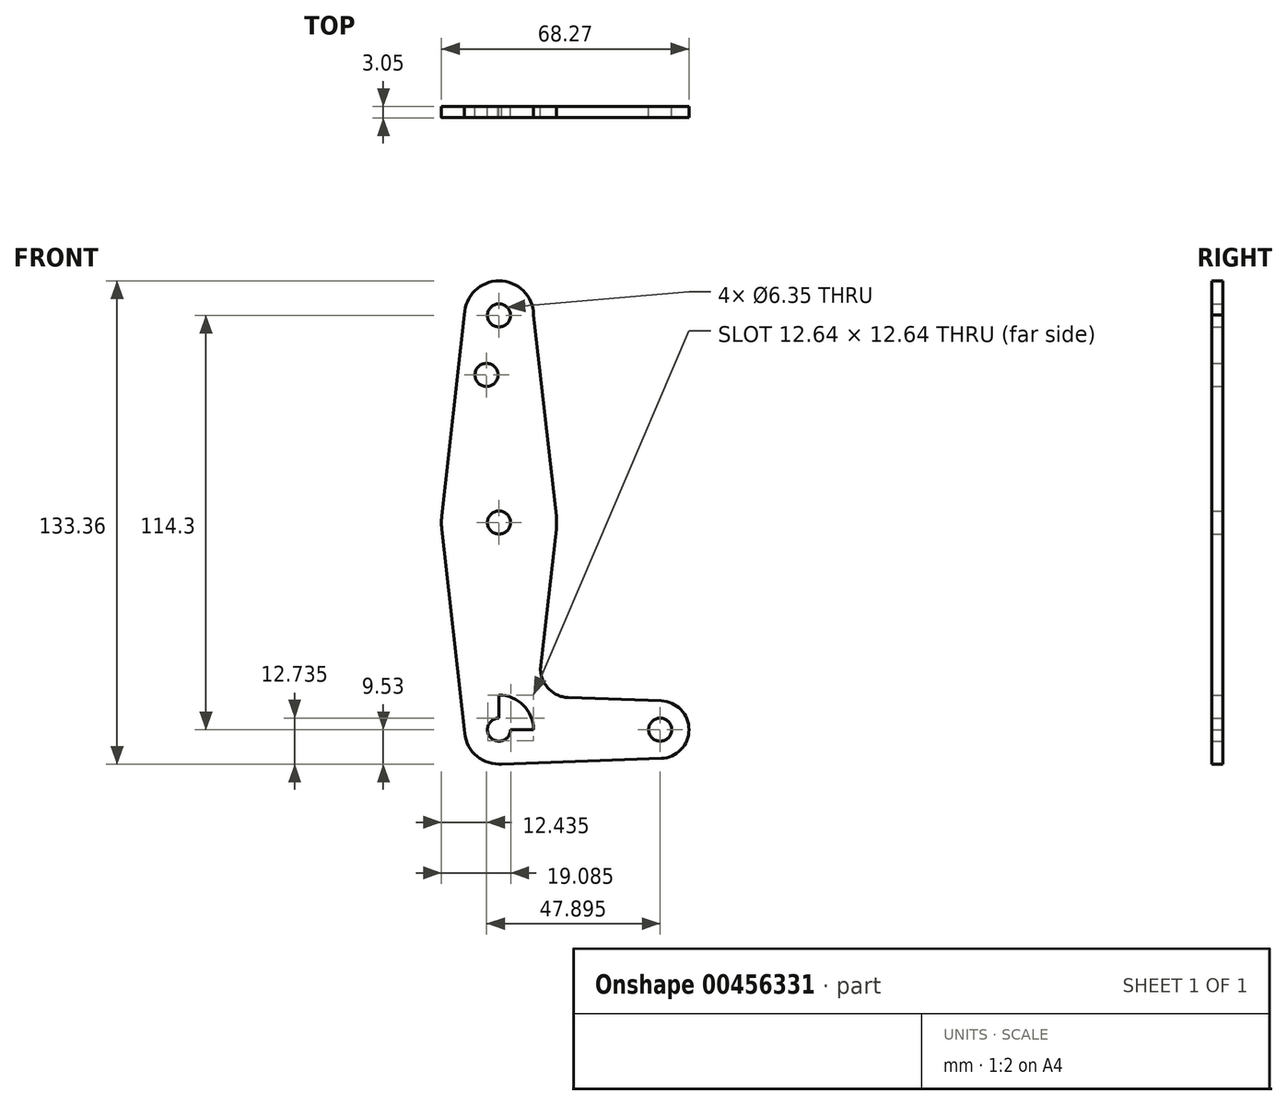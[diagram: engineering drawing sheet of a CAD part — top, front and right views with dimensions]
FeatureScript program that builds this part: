
annotation { "Feature Type Name" : "Feature", "Feature Type Description" : "" }
export const myFeature = defineFeature(function(context is Context, id is Id, definition is map)
    precondition{}
    {
        {
            var Q0;
            Q0=qCreatedBy(makeId("Front.planeOp"),FACE);
            var sketch = newSketch(context, id + "F0", { "sketchPlane" : qUnion([Q0])});
            skCircle(sketch, "E0", {"center": v(0, 0) * mm, "radius": 9.53 * mm});
            skLineSegment(sketch, "E1", {"start": v(0, 0) * mm, "end": v(44.45, 0) * mm});
            skLineSegment(sketch, "E2", {"start": v(0, 114.3) * mm, "end": v(0, 0) * mm});
            skCircle(sketch, "E3", {"center": v(44.45, 0) * mm, "radius": 7.94 * mm});
            skCircle(sketch, "E4", {"center": v(0, 114.3) * mm, "radius": 9.53 * mm});
            skCircle(sketch, "E5", {"center": v(0, 57.15) * mm, "radius": 15.88 * mm});
            skLineSegment(sketch, "E6", {"start": v(19.12, 8.84) * mm, "end": v(44.73, 7.93) * mm});
            skLineSegment(sketch, "E7", {"start": v(0, -9.53) * mm, "end": v(44.73, -7.93) * mm});
            skLineSegment(sketch, "E8", {"start": v(-9.52, 114.5) * mm, "end": v(-15.78, 58.93) * mm});
            skLineSegment(sketch, "E9", {"start": v(9.52, 114.47) * mm, "end": v(15.78, 58.93) * mm});
            skLineSegment(sketch, "E10", {"start": v(11.5, 17.68) * mm, "end": v(15.77, 55.37) * mm});
            skLineSegment(sketch, "E11", {"start": v(-9.53, 0) * mm, "end": v(-15.77, 55.37) * mm});
            skCircle(sketch, "E12", {"center": v(0, 114.3) * mm, "radius": 3.18 * mm});
            skCircle(sketch, "E13", {"center": v(44.45, 0) * mm, "radius": 3.18 * mm});
            skCircle(sketch, "E14", {"center": v(0, 0) * mm, "radius": 3.18 * mm});
            skCircle(sketch, "E15", {"center": v(0, 57.15) * mm, "radius": 3.18 * mm});
            skPoint(sketch, "E16.newPointA", {"position": v(9.52, 0.22) * mm});
            skArc(sketch, "E16.filletArc", {"start": v(11.5, 17.68) * mm, "mid": v(13.38, 11.6) * mm, "end": v(19.12, 8.84) * mm});
            skLineSegment(sketch, "E17", {"start": v(0, 0) * mm, "end": v(0, 57.15) * mm});
            skLineSegment(sketch, "E18", {"start": v(0, 57.15) * mm, "end": v(0, 0) * mm, "construction": true});
            skCircle(sketch, "E19", {"center": v(-3.44, 97.87) * mm, "radius": 3.18 * mm});
            skSolve(sketch);
        }
        {
            var Q0;
            Q0 = qSketchRegion(id + "F0", true);
            extrude(context, id + "F1", {"entities" : qUnion([Q0]), "depth" : 3.05 * mm});
        }
        {
            var Q0;
            {var subQ0=sQuery(id+"F0.wireOp",EDGE,"E17");var subQ1=sQuery(id+"F0.wireOp",EDGE,"E0");var subQ2=makeQuery(id+"F0.imprint","INTERSECT",VERTEX,{"derivedFrom":[subQ1,subQ0]});Q0=makeQuery(id+"F0.imprint","IMPRINT",FACE,{"disambiguationData":[TD([[makeQuery(id+"F0.imprint","IMPRINT",EDGE,{"disambiguationData":[TD([[subQ2,1.0]])],"derivedFrom":subQ1}),1.0]])]});}
            extrude(context, id + "F2", {"entities" : qUnion([Q0]), "operationType" : NewBodyOperationType.ADD, "depth" : 3.05 * mm});
        }
    });
